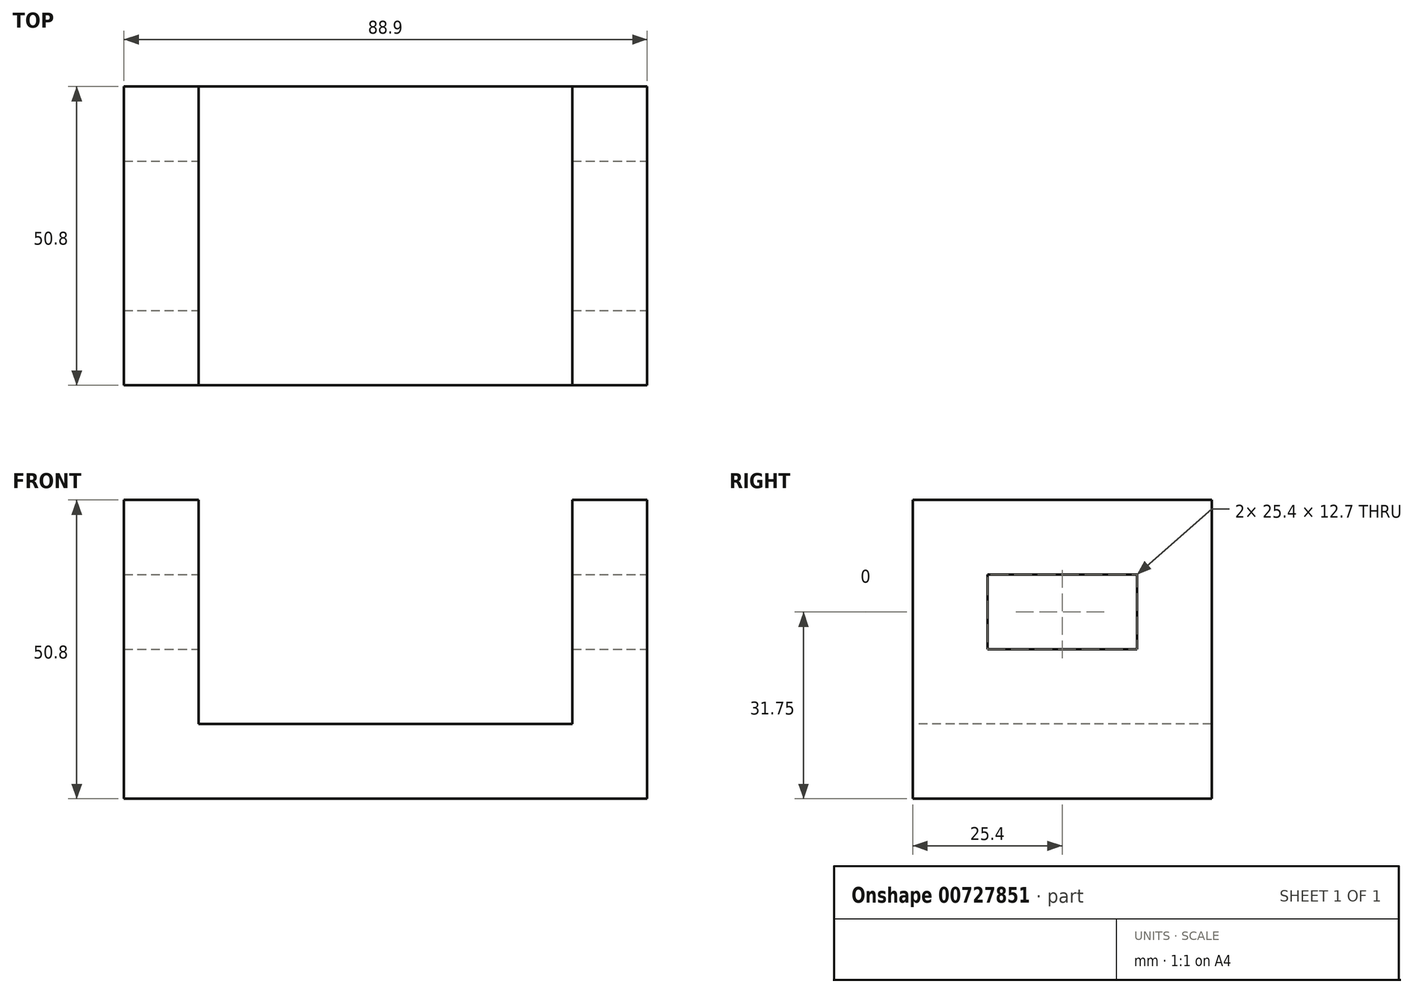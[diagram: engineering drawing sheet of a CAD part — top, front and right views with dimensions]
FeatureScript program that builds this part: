
annotation { "Feature Type Name" : "Feature", "Feature Type Description" : "" }
export const myFeature = defineFeature(function(context is Context, id is Id, definition is map)
    precondition{}
    {
        {
            var Q0;
            Q0=qCreatedBy(makeId("Right.planeOp"),FACE);
            var sketch = newSketch(context, id + "F0", { "sketchPlane" : qUnion([Q0])});
            skLineSegment(sketch, "E0.bottom", {"start": v(25.4, 25.4) * mm, "end": v(-25.4, 25.4) * mm});
            skLineSegment(sketch, "E0.top", {"start": v(25.4, -25.4) * mm, "end": v(-25.4, -25.4) * mm});
            skLineSegment(sketch, "E0.left", {"start": v(25.4, 25.4) * mm, "end": v(25.4, -25.4) * mm});
            skLineSegment(sketch, "E0.right", {"start": v(-25.4, 25.4) * mm, "end": v(-25.4, -25.4) * mm});
            skPoint(sketch, "E0.middle", {"position": v(0, 0) * mm});
            skSolve(sketch);
        }
        {
            var Q0;
            Q0=makeQuery(id+"F0.imprint","IMPRINT",FACE,{"disambiguationData":[TD([[makeQuery(id+"F0.imprint","IMPRINT",EDGE,{"derivedFrom":sQuery(id+"F0.wireOp",EDGE,"E0.bottom")}),1.0]])]});
            var sketch = newSketch(context, id + "F1", { "sketchPlane" : qUnion([Q0])});
            skLineSegment(sketch, "E1.bottom", {"start": v(12.7, 12.7) * mm, "end": v(-12.7, 12.7) * mm});
            skLineSegment(sketch, "E1.left", {"start": v(12.7, 12.7) * mm, "end": v(12.7, 0) * mm});
            skLineSegment(sketch, "E1.right", {"start": v(-12.7, 12.7) * mm, "end": v(-12.7, 0) * mm});
            skPoint(sketch, "E1.middle", {"position": v(0, 0) * mm});
            skLineSegment(sketch, "E2", {"start": v(-12.7, 0) * mm, "end": v(12.7, 0) * mm});
            skPoint(sketch, "E3.start.orphan", {"position": v(0, -25.4) * mm});
            skPoint(sketch, "E4.orphan", {"position": v(12.7, -12.7) * mm});
            skPoint(sketch, "E5.orphan", {"position": v(-12.7, -12.7) * mm});
            skSolve(sketch);
        }
        {
            var Q0;
            Q0=makeQuery(id+"F0.imprint","IMPRINT",FACE,{"disambiguationData":[TD([[makeQuery(id+"F0.imprint","IMPRINT",EDGE,{"derivedFrom":sQuery(id+"F0.wireOp",EDGE,"E0.bottom")}),1.0]])]});
            extrude(context, id + "F2", {"entities" : qUnion([Q0]), "oppositeDirection" : true, "depth" : 88.9 * mm, "offsetDistance" : 25.4 * mm});
        }
        {
            var Q0;
            Q0=makeQuery(id+"F1.imprint","IMPRINT",FACE,{"disambiguationData":[TD([[makeQuery(id+"F1.imprint","IMPRINT",EDGE,{"derivedFrom":sQuery(id+"F1.wireOp",EDGE,"E1.bottom")}),1.0]])]});
            extrude(context, id + "F3", {"entities" : qUnion([Q0]), "operationType" : NewBodyOperationType.REMOVE, "endBound" : BoundingType.THROUGH_ALL, "oppositeDirection" : true, "depth" : 25.4 * mm, "offsetDistance" : 25.4 * mm});
        }
        {
            var Q0;
            Q0=makeQuery(id+"F2.opExtrude","SWEPT_FACE",FACE,{"disambiguationData":[OSD([sQuery(id+"F0.wireOp",EDGE,"E0.right")])]});
            var sketch = newSketch(context, id + "F4", { "sketchPlane" : qUnion([Q0])});
            skLineSegment(sketch, "E6", {"start": v(-88.9, -12.7) * mm, "end": v(0, -12.7) * mm});
            skPoint(sketch, "E7.end.orphan", {"position": v(-44.45, -25.4) * mm});
            skPoint(sketch, "E7.start.orphan", {"position": v(-44.45, -12.7) * mm});
            skLineSegment(sketch, "E8", {"start": v(-12.7, 25.4) * mm, "end": v(-12.7, -12.7) * mm});
            skLineSegment(sketch, "E9", {"start": v(-76.2, -12.7) * mm, "end": v(-76.2, 25.4) * mm});
            skSolve(sketch);
        }
        {
            var Q0;
            {var subQ0=sQuery(id+"F4.wireOp",EDGE,"E8");Q0=makeQuery(id+"F4.imprint","IMPRINT",FACE,{"disambiguationData":[TD([[makeQuery(id+"F4.imprint","IMPRINT",EDGE,{"derivedFrom":subQ0}),-1.0]])]});}
            extrude(context, id + "F5", {"entities" : qUnion([Q0]), "operationType" : NewBodyOperationType.REMOVE, "endBound" : BoundingType.THROUGH_ALL, "oppositeDirection" : true, "depth" : 50.8 * mm, "offsetDistance" : 25.4 * mm});
        }
    });
